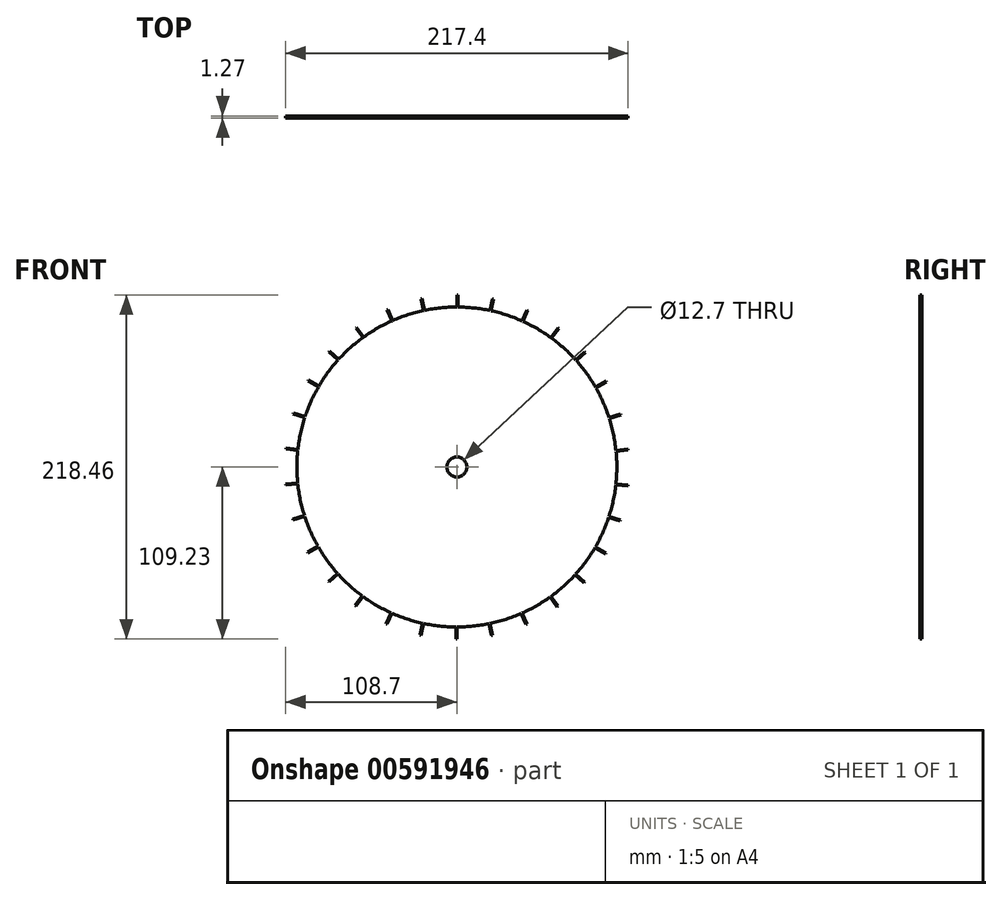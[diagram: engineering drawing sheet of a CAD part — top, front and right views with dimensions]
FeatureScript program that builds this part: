
annotation { "Feature Type Name" : "Feature", "Feature Type Description" : "" }
export const myFeature = defineFeature(function(context is Context, id is Id, definition is map)
    precondition{}
    {
        {
            var Q0;
            Q0=qCreatedBy(makeId("Front.planeOp"),FACE);
            var sketch = newSketch(context, id + "F0", { "sketchPlane" : qUnion([Q0])});
            skLineSegment(sketch, "E0", {"start": v(0, 122.37) * mm, "end": v(0, -114.94) * mm});
            skLineSegment(sketch, "E1", {"start": v(-143.5, 0) * mm, "end": v(162.63, 0) * mm});
            skCircle(sketch, "E2", {"center": v(0, 0) * mm, "radius": 6.35 * mm});
            skCircle(sketch, "E3", {"center": v(0, 0) * mm, "radius": 101.6 * mm});
            skLineSegment(sketch, "E4", {"start": v(0, 109.23) * mm, "end": v(0, 92.95) * mm});
            skLineSegment(sketch, "E5.1.0", {"start": v(-22.71, 106.84) * mm, "end": v(-19.33, 90.92) * mm});
            skLineSegment(sketch, "E5.2.0", {"start": v(-44.43, 99.79) * mm, "end": v(-37.8, 84.92) * mm});
            skLineSegment(sketch, "E5.3.0", {"start": v(-64.2, 88.37) * mm, "end": v(-54.64, 75.2) * mm});
            skLineSegment(sketch, "E5.4.0", {"start": v(-81.17, 73.1) * mm, "end": v(-69.08, 62.2) * mm});
            skLineSegment(sketch, "E5.5.0", {"start": v(-94.6, 54.62) * mm, "end": v(-80.5, 46.48) * mm});
            skLineSegment(sketch, "E5.6.0", {"start": v(-103.89, 33.75) * mm, "end": v(-88.4, 28.72) * mm});
            skLineSegment(sketch, "E5.7.0", {"start": v(-108.63, 11.42) * mm, "end": v(-92.44, 9.72) * mm});
            skLineSegment(sketch, "E5.8.0", {"start": v(-108.63, -11.42) * mm, "end": v(-92.44, -9.72) * mm});
            skLineSegment(sketch, "E5.9.0", {"start": v(-103.89, -33.75) * mm, "end": v(-88.4, -28.72) * mm});
            skLineSegment(sketch, "E5.10.0", {"start": v(-94.6, -54.62) * mm, "end": v(-80.5, -46.48) * mm});
            skLineSegment(sketch, "E5.11.0", {"start": v(-81.17, -73.1) * mm, "end": v(-69.08, -62.2) * mm});
            skLineSegment(sketch, "E5.12.0", {"start": v(-64.2, -88.37) * mm, "end": v(-54.64, -75.2) * mm});
            skLineSegment(sketch, "E5.13.0", {"start": v(-44.43, -99.79) * mm, "end": v(-37.8, -84.92) * mm});
            skLineSegment(sketch, "E5.14.0", {"start": v(-22.71, -106.84) * mm, "end": v(-19.33, -90.92) * mm});
            skLineSegment(sketch, "E5.15.0", {"start": v(0, -109.23) * mm, "end": v(0, -92.95) * mm});
            skLineSegment(sketch, "E5.16.0", {"start": v(22.71, -106.84) * mm, "end": v(19.33, -90.92) * mm});
            skLineSegment(sketch, "E5.17.0", {"start": v(44.43, -99.79) * mm, "end": v(37.8, -84.92) * mm});
            skLineSegment(sketch, "E5.18.0", {"start": v(64.2, -88.37) * mm, "end": v(54.64, -75.2) * mm});
            skLineSegment(sketch, "E5.19.0", {"start": v(81.17, -73.1) * mm, "end": v(69.08, -62.2) * mm});
            skLineSegment(sketch, "E5.20.0", {"start": v(94.6, -54.62) * mm, "end": v(80.5, -46.48) * mm});
            skLineSegment(sketch, "E5.21.0", {"start": v(103.89, -33.75) * mm, "end": v(88.4, -28.72) * mm});
            skLineSegment(sketch, "E5.22.0", {"start": v(108.63, -11.42) * mm, "end": v(92.44, -9.72) * mm});
            skLineSegment(sketch, "E5.23.0", {"start": v(108.63, 11.42) * mm, "end": v(92.44, 9.72) * mm});
            skLineSegment(sketch, "E5.24.0", {"start": v(103.89, 33.75) * mm, "end": v(88.4, 28.72) * mm});
            skLineSegment(sketch, "E5.25.0", {"start": v(94.6, 54.62) * mm, "end": v(80.5, 46.48) * mm});
            skLineSegment(sketch, "E5.26.0", {"start": v(81.17, 73.1) * mm, "end": v(69.08, 62.2) * mm});
            skLineSegment(sketch, "E5.27.0", {"start": v(64.2, 88.37) * mm, "end": v(54.64, 75.2) * mm});
            skLineSegment(sketch, "E5.28.0", {"start": v(44.43, 99.79) * mm, "end": v(37.8, 84.92) * mm});
            skLineSegment(sketch, "E5.29.0", {"start": v(22.71, 106.84) * mm, "end": v(19.33, 90.92) * mm});
            skLineSegment(sketch, "E6", {"start": v(0, 109.23) * mm, "end": v(0.64, 109.23) * mm});
            skLineSegment(sketch, "E7", {"start": v(0.64, 109.23) * mm, "end": v(0.64, 92.95) * mm});
            skLineSegment(sketch, "E8", {"start": v(0.64, 92.95) * mm, "end": v(0, 92.95) * mm});
            skLineSegment(sketch, "E9.1.0", {"start": v(-22.09, 106.98) * mm, "end": v(-18.7, 91.05) * mm});
            skLineSegment(sketch, "E9.1.2", {"start": v(-18.7, 91.05) * mm, "end": v(-19.33, 90.92) * mm});
            skLineSegment(sketch, "E9.1.3", {"start": v(-22.71, 106.84) * mm, "end": v(-22.09, 106.98) * mm});
            skLineSegment(sketch, "E9.2.0", {"start": v(-43.85, 100.05) * mm, "end": v(-37.23, 85.18) * mm});
            skLineSegment(sketch, "E9.2.2", {"start": v(-37.23, 85.18) * mm, "end": v(-37.8, 84.92) * mm});
            skLineSegment(sketch, "E9.2.3", {"start": v(-44.43, 99.79) * mm, "end": v(-43.85, 100.05) * mm});
            skLineSegment(sketch, "E9.3.0", {"start": v(-63.7, 88.74) * mm, "end": v(-54.12, 75.57) * mm});
            skLineSegment(sketch, "E9.3.2", {"start": v(-54.12, 75.57) * mm, "end": v(-54.64, 75.2) * mm});
            skLineSegment(sketch, "E9.3.3", {"start": v(-64.2, 88.37) * mm, "end": v(-63.7, 88.74) * mm});
            skLineSegment(sketch, "E9.4.0", {"start": v(-80.75, 73.56) * mm, "end": v(-68.65, 62.67) * mm});
            skLineSegment(sketch, "E9.4.2", {"start": v(-68.65, 62.67) * mm, "end": v(-69.08, 62.2) * mm});
            skLineSegment(sketch, "E9.4.3", {"start": v(-81.17, 73.1) * mm, "end": v(-80.75, 73.56) * mm});
            skLineSegment(sketch, "E9.5.0", {"start": v(-94.28, 55.17) * mm, "end": v(-80.18, 47.03) * mm});
            skLineSegment(sketch, "E9.5.2", {"start": v(-80.18, 47.03) * mm, "end": v(-80.5, 46.48) * mm});
            skLineSegment(sketch, "E9.5.3", {"start": v(-94.6, 54.62) * mm, "end": v(-94.28, 55.17) * mm});
            skLineSegment(sketch, "E9.6.0", {"start": v(-103.69, 34.36) * mm, "end": v(-88.2, 29.33) * mm});
            skLineSegment(sketch, "E9.6.2", {"start": v(-88.2, 29.33) * mm, "end": v(-88.4, 28.72) * mm});
            skLineSegment(sketch, "E9.6.3", {"start": v(-103.89, 33.75) * mm, "end": v(-103.69, 34.36) * mm});
            skLineSegment(sketch, "E9.7.0", {"start": v(-108.57, 12.05) * mm, "end": v(-92.38, 10.35) * mm});
            skLineSegment(sketch, "E9.7.2", {"start": v(-92.38, 10.35) * mm, "end": v(-92.44, 9.72) * mm});
            skLineSegment(sketch, "E9.7.3", {"start": v(-108.63, 11.42) * mm, "end": v(-108.57, 12.05) * mm});
            skLineSegment(sketch, "E9.8.0", {"start": v(-108.7, -10.79) * mm, "end": v(-92.51, -9.08) * mm});
            skLineSegment(sketch, "E9.8.2", {"start": v(-92.51, -9.08) * mm, "end": v(-92.44, -9.72) * mm});
            skLineSegment(sketch, "E9.8.3", {"start": v(-108.63, -11.42) * mm, "end": v(-108.7, -10.79) * mm});
            skLineSegment(sketch, "E9.9.0", {"start": v(-104.08, -33.15) * mm, "end": v(-88.6, -28.12) * mm});
            skLineSegment(sketch, "E9.9.2", {"start": v(-88.6, -28.12) * mm, "end": v(-88.4, -28.72) * mm});
            skLineSegment(sketch, "E9.9.3", {"start": v(-103.89, -33.75) * mm, "end": v(-104.08, -33.15) * mm});
            skLineSegment(sketch, "E9.10.0", {"start": v(-94.91, -54.07) * mm, "end": v(-80.82, -45.93) * mm});
            skLineSegment(sketch, "E9.10.2", {"start": v(-80.82, -45.93) * mm, "end": v(-80.5, -46.48) * mm});
            skLineSegment(sketch, "E9.10.3", {"start": v(-94.6, -54.62) * mm, "end": v(-94.91, -54.07) * mm});
            skLineSegment(sketch, "E9.11.0", {"start": v(-81.6, -72.62) * mm, "end": v(-69.5, -61.73) * mm});
            skLineSegment(sketch, "E9.11.2", {"start": v(-69.5, -61.73) * mm, "end": v(-69.08, -62.2) * mm});
            skLineSegment(sketch, "E9.11.3", {"start": v(-81.17, -73.1) * mm, "end": v(-81.6, -72.62) * mm});
            skLineSegment(sketch, "E9.12.0", {"start": v(-64.72, -88) * mm, "end": v(-55.15, -74.83) * mm});
            skLineSegment(sketch, "E9.12.2", {"start": v(-55.15, -74.83) * mm, "end": v(-54.64, -75.2) * mm});
            skLineSegment(sketch, "E9.12.3", {"start": v(-64.2, -88.37) * mm, "end": v(-64.72, -88) * mm});
            skLineSegment(sketch, "E9.13.0", {"start": v(-45, -99.53) * mm, "end": v(-38.39, -84.66) * mm});
            skLineSegment(sketch, "E9.13.2", {"start": v(-38.39, -84.66) * mm, "end": v(-37.8, -84.92) * mm});
            skLineSegment(sketch, "E9.13.3", {"start": v(-44.43, -99.79) * mm, "end": v(-45, -99.53) * mm});
            skLineSegment(sketch, "E9.14.0", {"start": v(-23.33, -106.71) * mm, "end": v(-19.95, -90.8) * mm});
            skLineSegment(sketch, "E9.14.2", {"start": v(-19.95, -90.8) * mm, "end": v(-19.33, -90.92) * mm});
            skLineSegment(sketch, "E9.14.3", {"start": v(-22.71, -106.84) * mm, "end": v(-23.33, -106.71) * mm});
            skLineSegment(sketch, "E9.15.0", {"start": v(-0.64, -109.23) * mm, "end": v(-0.64, -92.95) * mm});
            skLineSegment(sketch, "E9.15.2", {"start": v(-0.64, -92.95) * mm, "end": v(0, -92.95) * mm});
            skLineSegment(sketch, "E9.15.3", {"start": v(0, -109.23) * mm, "end": v(-0.64, -109.23) * mm});
            skLineSegment(sketch, "E9.16.0", {"start": v(22.09, -106.98) * mm, "end": v(18.7, -91.05) * mm});
            skLineSegment(sketch, "E9.16.2", {"start": v(18.7, -91.05) * mm, "end": v(19.33, -90.92) * mm});
            skLineSegment(sketch, "E9.16.3", {"start": v(22.71, -106.84) * mm, "end": v(22.09, -106.98) * mm});
            skLineSegment(sketch, "E9.17.0", {"start": v(43.85, -100.05) * mm, "end": v(37.23, -85.18) * mm});
            skLineSegment(sketch, "E9.17.2", {"start": v(37.23, -85.18) * mm, "end": v(37.8, -84.92) * mm});
            skLineSegment(sketch, "E9.17.3", {"start": v(44.43, -99.79) * mm, "end": v(43.85, -100.05) * mm});
            skLineSegment(sketch, "E9.18.0", {"start": v(63.7, -88.74) * mm, "end": v(54.12, -75.57) * mm});
            skLineSegment(sketch, "E9.18.2", {"start": v(54.12, -75.57) * mm, "end": v(54.64, -75.2) * mm});
            skLineSegment(sketch, "E9.18.3", {"start": v(64.2, -88.37) * mm, "end": v(63.7, -88.74) * mm});
            skLineSegment(sketch, "E9.19.0", {"start": v(80.75, -73.56) * mm, "end": v(68.65, -62.67) * mm});
            skLineSegment(sketch, "E9.19.2", {"start": v(68.65, -62.67) * mm, "end": v(69.08, -62.2) * mm});
            skLineSegment(sketch, "E9.19.3", {"start": v(81.17, -73.1) * mm, "end": v(80.75, -73.56) * mm});
            skLineSegment(sketch, "E9.20.0", {"start": v(94.28, -55.17) * mm, "end": v(80.18, -47.03) * mm});
            skLineSegment(sketch, "E9.20.2", {"start": v(80.18, -47.03) * mm, "end": v(80.5, -46.48) * mm});
            skLineSegment(sketch, "E9.20.3", {"start": v(94.6, -54.62) * mm, "end": v(94.28, -55.17) * mm});
            skLineSegment(sketch, "E9.21.0", {"start": v(103.69, -34.36) * mm, "end": v(88.2, -29.33) * mm});
            skLineSegment(sketch, "E9.21.2", {"start": v(88.2, -29.33) * mm, "end": v(88.4, -28.72) * mm});
            skLineSegment(sketch, "E9.21.3", {"start": v(103.89, -33.75) * mm, "end": v(103.69, -34.36) * mm});
            skLineSegment(sketch, "E9.22.0", {"start": v(108.57, -12.05) * mm, "end": v(92.38, -10.35) * mm});
            skLineSegment(sketch, "E9.22.2", {"start": v(92.38, -10.35) * mm, "end": v(92.44, -9.72) * mm});
            skLineSegment(sketch, "E9.22.3", {"start": v(108.63, -11.42) * mm, "end": v(108.57, -12.05) * mm});
            skLineSegment(sketch, "E9.23.0", {"start": v(108.7, 10.79) * mm, "end": v(92.51, 9.08) * mm});
            skLineSegment(sketch, "E9.23.2", {"start": v(92.51, 9.08) * mm, "end": v(92.44, 9.72) * mm});
            skLineSegment(sketch, "E9.23.3", {"start": v(108.63, 11.42) * mm, "end": v(108.7, 10.79) * mm});
            skLineSegment(sketch, "E9.24.0", {"start": v(104.08, 33.15) * mm, "end": v(88.6, 28.12) * mm});
            skLineSegment(sketch, "E9.24.2", {"start": v(88.6, 28.12) * mm, "end": v(88.4, 28.72) * mm});
            skLineSegment(sketch, "E9.24.3", {"start": v(103.89, 33.75) * mm, "end": v(104.08, 33.15) * mm});
            skLineSegment(sketch, "E9.25.0", {"start": v(94.91, 54.07) * mm, "end": v(80.82, 45.93) * mm});
            skLineSegment(sketch, "E9.25.2", {"start": v(80.82, 45.93) * mm, "end": v(80.5, 46.48) * mm});
            skLineSegment(sketch, "E9.25.3", {"start": v(94.6, 54.62) * mm, "end": v(94.91, 54.07) * mm});
            skLineSegment(sketch, "E9.26.0", {"start": v(81.6, 72.62) * mm, "end": v(69.5, 61.73) * mm});
            skLineSegment(sketch, "E9.26.2", {"start": v(69.5, 61.73) * mm, "end": v(69.08, 62.2) * mm});
            skLineSegment(sketch, "E9.26.3", {"start": v(81.17, 73.1) * mm, "end": v(81.6, 72.62) * mm});
            skLineSegment(sketch, "E9.27.0", {"start": v(64.72, 88) * mm, "end": v(55.15, 74.83) * mm});
            skLineSegment(sketch, "E9.27.2", {"start": v(55.15, 74.83) * mm, "end": v(54.64, 75.2) * mm});
            skLineSegment(sketch, "E9.27.3", {"start": v(64.2, 88.37) * mm, "end": v(64.72, 88) * mm});
            skLineSegment(sketch, "E9.28.0", {"start": v(45, 99.53) * mm, "end": v(38.39, 84.66) * mm});
            skLineSegment(sketch, "E9.28.2", {"start": v(38.39, 84.66) * mm, "end": v(37.8, 84.92) * mm});
            skLineSegment(sketch, "E9.28.3", {"start": v(44.43, 99.79) * mm, "end": v(45, 99.53) * mm});
            skLineSegment(sketch, "E9.29.0", {"start": v(23.33, 106.71) * mm, "end": v(19.95, 90.8) * mm});
            skLineSegment(sketch, "E9.29.2", {"start": v(19.95, 90.8) * mm, "end": v(19.33, 90.92) * mm});
            skLineSegment(sketch, "E9.29.3", {"start": v(22.71, 106.84) * mm, "end": v(23.33, 106.71) * mm});
            skPoint(sketch, "E10", {"position": v(0, 101.6) * mm});
            skPoint(sketch, "E11.1.0", {"position": v(-87.99, -50.8) * mm});
            skPoint(sketch, "E11.2.0", {"position": v(87.99, -50.8) * mm});
            skSolve(sketch);
        }
        {
            var Q0;
            Q0 = qSketchRegion(id + "F0", true);
            extrude(context, id + "F1", {"entities" : qUnion([Q0]), "depth" : 1.27 * mm, "offsetDistance" : 25.4 * mm});
        }
    });
